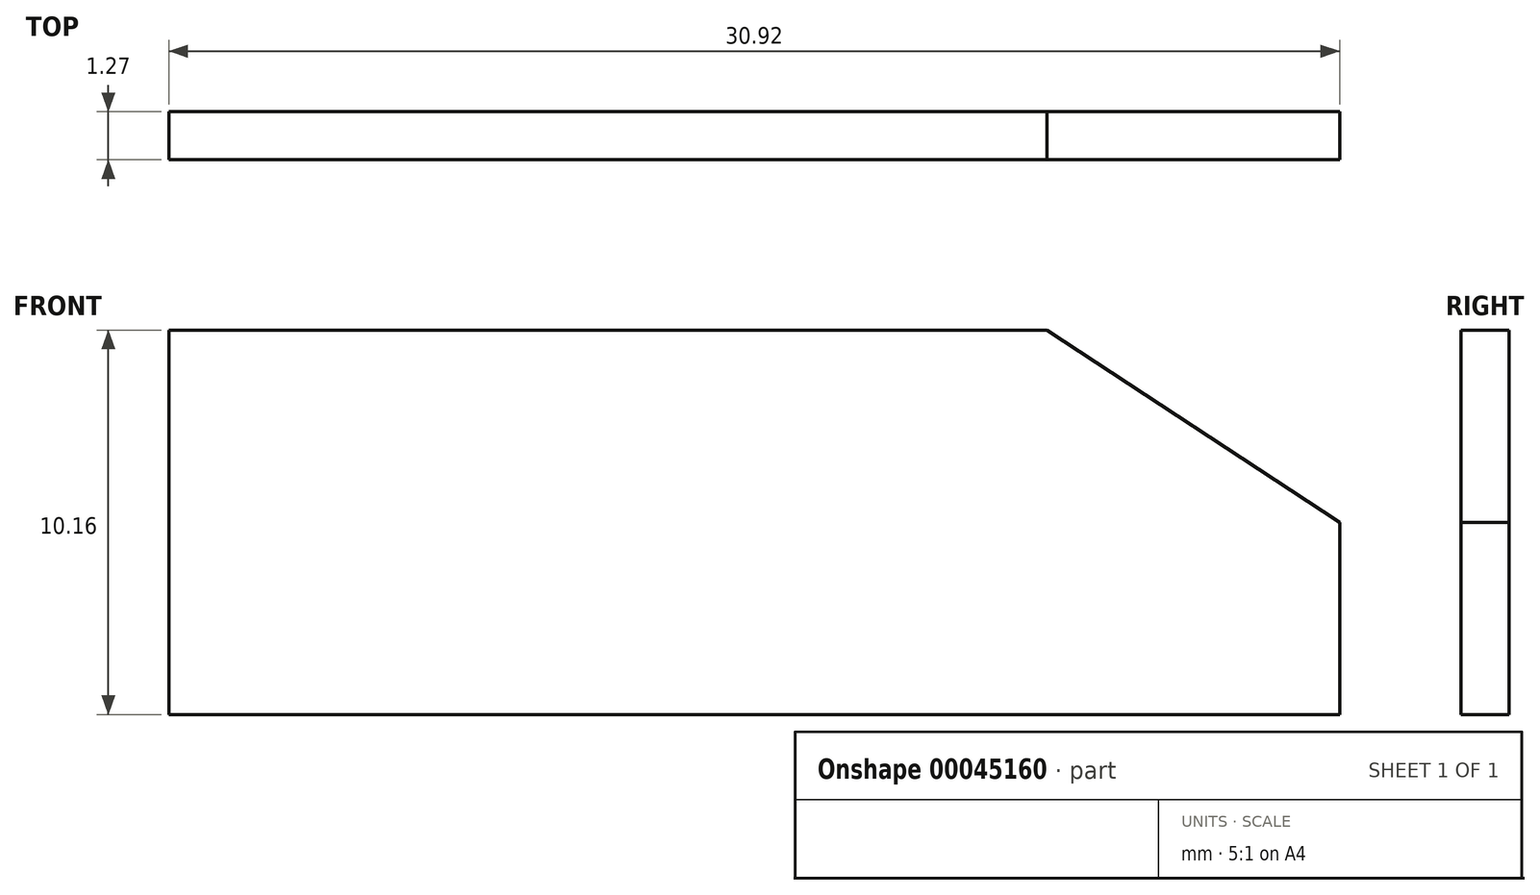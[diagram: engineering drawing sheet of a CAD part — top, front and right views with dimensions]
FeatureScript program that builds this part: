
annotation { "Feature Type Name" : "Feature", "Feature Type Description" : "" }
export const myFeature = defineFeature(function(context is Context, id is Id, definition is map)
    precondition{}
    {
        {
            var Q0;
            Q0=qCreatedBy(makeId("Front.planeOp"),FACE);
            var sketch = newSketch(context, id + "F0", { "sketchPlane" : qUnion([Q0])});
            skLineSegment(sketch, "E0", {"start": v(0, 0) * mm, "end": v(30.92, 0) * mm});
            skLineSegment(sketch, "E1", {"start": v(0, 10.16) * mm, "end": v(0, 0) * mm});
            skLineSegment(sketch, "E2", {"start": v(15.46, 10.16) * mm, "end": v(23.2, 10.16) * mm});
            skLineSegment(sketch, "E3", {"start": v(23.2, 10.16) * mm, "end": v(30.92, 5.08) * mm});
            skLineSegment(sketch, "E4", {"start": v(30.92, 5.08) * mm, "end": v(30.92, 0) * mm});
            skLineSegment(sketch, "E5", {"start": v(23.2, 10.16) * mm, "end": v(0, 10.16) * mm});
            skSolve(sketch);
        }
        {
            var Q0;
            Q0 = qSketchRegion(id + "F0", true);
            extrude(context, id + "F1", {"entities" : qUnion([Q0]), "depth" : 1.27 * mm});
        }
    });
